# Revit family: Express Devens Side Chairs
name_source: partatom
category: Furniture
units: mm (PartAtom-declared; Revit-internal decimal feet)

## family parameters
Always vertical = Yes
Cut with Voids When Loaded = No
OmniClass Number = 23.40.20.00
OmniClass Title = General Furniture and Specialties
Room Calculation Point = No
Shared = No
Work Plane-Based = No

## types (4) — shared parameters
Default Elevation = 0' - 0"
Manufacturer = AIS Inc
Product = EXPRESS DEVENS SIDE CHAIRS
URL = https://www.ais-inc.com

## per-type parameters (varying)
| type | 4657 | 4657C | 4667 | 4667C | Description |
| 4657 | Yes | No | No | No | Black Side Chair (Express) |
| 4657C | No | Yes | No | No | Configurable Black Side Chair |
| 4667 | No | No | Yes | No | Grey Side Chair (Express) |
| 4667C | No | No | No | Yes | Configurable Grey Side Chair |

note: column(s) folded — value = type name in every type: Model

## geometry (parser evidence)
native form markers: Sweep x3
no freeform markers — native parametric forms only
